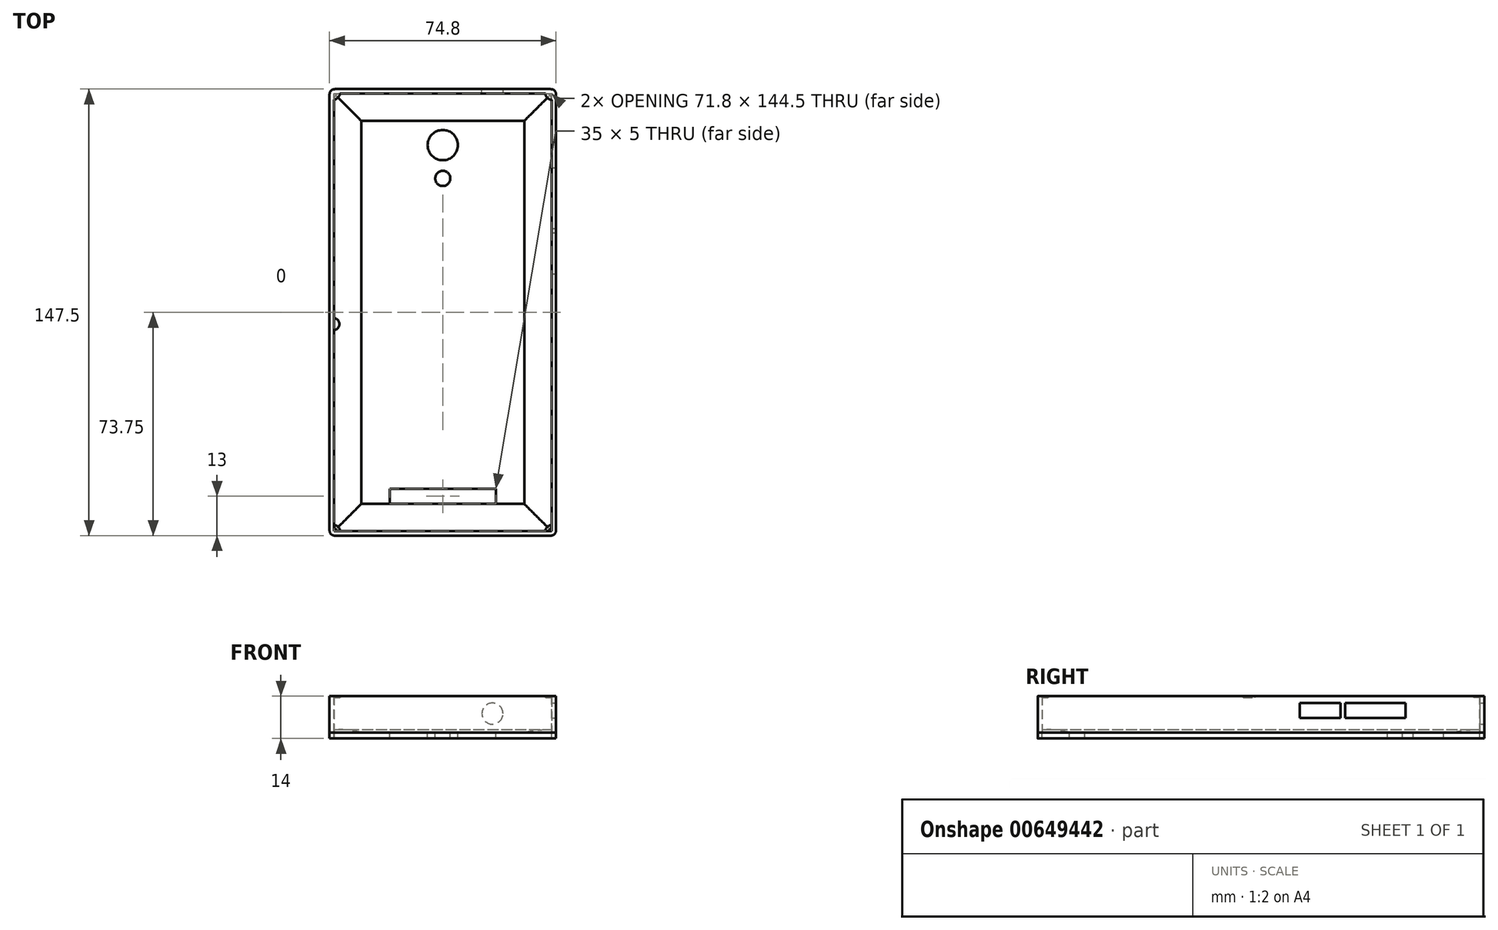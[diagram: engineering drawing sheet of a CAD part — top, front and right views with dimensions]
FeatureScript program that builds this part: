
annotation { "Feature Type Name" : "Feature", "Feature Type Description" : "" }
export const myFeature = defineFeature(function(context is Context, id is Id, definition is map)
    precondition{}
    {
        {
            var Q0;
            Q0=qCreatedBy(makeId("Top.planeOp"),FACE);
            var sketch = newSketch(context, id + "F0", { "sketchPlane" : qUnion([Q0])});
            skLineSegment(sketch, "E0.bottom", {"start": v(0, 0) * mm, "end": v(71.8, 0) * mm});
            skLineSegment(sketch, "E0.top", {"start": v(0, 144.5) * mm, "end": v(71.8, 144.5) * mm});
            skLineSegment(sketch, "E0.left", {"start": v(0, 0) * mm, "end": v(0, 144.5) * mm});
            skLineSegment(sketch, "E0.right", {"start": v(71.8, 0) * mm, "end": v(71.8, 144.5) * mm});
            skLineSegment(sketch, "E1", {"start": v(35.9, 9) * mm, "end": v(53.4, 9) * mm});
            skLineSegment(sketch, "E2", {"start": v(53.4, 9) * mm, "end": v(18.4, 9) * mm});
            skLineSegment(sketch, "E3", {"start": v(18.4, 9) * mm, "end": v(18.4, 14) * mm});
            skLineSegment(sketch, "E4", {"start": v(18.4, 14) * mm, "end": v(53.4, 14) * mm});
            skLineSegment(sketch, "E5", {"start": v(53.4, 14) * mm, "end": v(53.4, 9) * mm});
            skCircle(sketch, "E6", {"center": v(35.9, 127.5) * mm, "radius": 5 * mm});
            skCircle(sketch, "E7", {"center": v(35.9, 116.5) * mm, "radius": 2.5 * mm});
            skLineSegment(sketch, "E8", {"start": v(9, 110.42) * mm, "end": v(9, 9) * mm});
            skLineSegment(sketch, "E9", {"start": v(9, 9) * mm, "end": v(62.8, 9) * mm});
            skLineSegment(sketch, "E10", {"start": v(62.8, 9) * mm, "end": v(62.8, 135.5) * mm});
            skLineSegment(sketch, "E11", {"start": v(62.8, 135.5) * mm, "end": v(9, 135.5) * mm});
            skLineSegment(sketch, "E12", {"start": v(9, 135.5) * mm, "end": v(9, 110.42) * mm});
            skLineSegment(sketch, "E13.0", {"start": v(-1.5, -1.5) * mm, "end": v(-1.5, 146) * mm});
            skLineSegment(sketch, "E13.1", {"start": v(-1.5, -1.5) * mm, "end": v(73.3, -1.5) * mm});
            skLineSegment(sketch, "E13.2", {"start": v(73.3, -1.5) * mm, "end": v(73.3, 146) * mm});
            skLineSegment(sketch, "E13.3", {"start": v(-1.5, 146) * mm, "end": v(73.3, 146) * mm});
            skSolve(sketch);
        }
        {
            var Q0;
            Q0=makeQuery(id+"F0.imprint","IMPRINT",FACE,{"disambiguationData":[TD([[makeQuery(id+"F0.imprint","IMPRINT",EDGE,{"derivedFrom":sQuery(id+"F0.wireOp",EDGE,"E0.bottom")}),-1.0]])]});
            extrude(context, id + "F1", {"entities" : qUnion([Q0]), "depth" : 12 * mm, "offsetDistance" : 25 * mm});
        }
        {
            var Q0;
            Q0=makeQuery(id+"F0.imprint","IMPRINT",FACE,{"disambiguationData":[TD([[makeQuery(id+"F0.imprint","IMPRINT",EDGE,{"derivedFrom":sQuery(id+"F0.wireOp",EDGE,"E0.bottom")}),1.0]])]});
            var Q1;
            {var subQ3=sQuery(id+"F0.wireOp",EDGE,"E3");Q1=makeQuery(id+"F0.imprint","IMPRINT",FACE,{"disambiguationData":[TD([[makeQuery(id+"F0.imprint","IMPRINT",EDGE,{"derivedFrom":subQ3}),1.0]])]});}
            extrude(context, id + "F2", {"entities" : qUnion([Q0, Q1]), "operationType" : NewBodyOperationType.ADD, "oppositeDirection" : true, "depth" : 2 * mm, "offsetDistance" : 25 * mm});
        }
        {
            var Q0;
            Q0=makeQuery(id+"F1.opExtrude","SWEPT_EDGE",EDGE,{"disambiguationData":[OSD([sQuery(id+"F0.wireOp",EDGE,"E13.0"),sQuery(id+"F0.wireOp",EDGE,"E13.3")])]});
            var Q1;
            Q1=makeQuery(id+"F1.opExtrude","SWEPT_EDGE",EDGE,{"disambiguationData":[OSD([sQuery(id+"F0.wireOp",EDGE,"E13.2"),sQuery(id+"F0.wireOp",EDGE,"E13.3")])]});
            var Q2;
            Q2=makeQuery(id+"F1.opExtrude","SWEPT_EDGE",EDGE,{"disambiguationData":[OSD([sQuery(id+"F0.wireOp",EDGE,"E13.1"),sQuery(id+"F0.wireOp",EDGE,"E13.2")])]});
            var Q3;
            Q3=makeQuery(id+"F1.opExtrude","SWEPT_EDGE",EDGE,{"disambiguationData":[OSD([sQuery(id+"F0.wireOp",EDGE,"E13.0"),sQuery(id+"F0.wireOp",EDGE,"E13.1")])]});
            var Q4;
            Q4=makeQuery(id+"F1.opExtrude","SWEPT_EDGE",EDGE,{"disambiguationData":[OSD([sQuery(id+"F0.wireOp",EDGE,"E0.bottom"),sQuery(id+"F0.wireOp",EDGE,"E0.left")])]});
            var Q5;
            Q5=makeQuery(id+"F1.opExtrude","SWEPT_EDGE",EDGE,{"disambiguationData":[OSD([sQuery(id+"F0.wireOp",EDGE,"E0.bottom"),sQuery(id+"F0.wireOp",EDGE,"E0.right")])]});
            var Q6;
            Q6=makeQuery(id+"F1.opExtrude","SWEPT_EDGE",EDGE,{"disambiguationData":[OSD([sQuery(id+"F0.wireOp",EDGE,"E0.top"),sQuery(id+"F0.wireOp",EDGE,"E0.right")])]});
            var Q7;
            Q7=makeQuery(id+"F1.opExtrude","SWEPT_EDGE",EDGE,{"disambiguationData":[OSD([sQuery(id+"F0.wireOp",EDGE,"E0.top"),sQuery(id+"F0.wireOp",EDGE,"E0.left")])]});
            fillet(context, id + "F3", {"entities" : qUnion([Q0, Q1, Q2, Q3, Q4, Q5, Q6, Q7]), "radius" : 2 * mm, "tangentPropagation" : true, "rho" : 0.5, "crossSection" : FilletCrossSection.CONIC, "allowEdgeOverflow" : false});
        }
        {
            var Q0;
            Q0=makeQuery(id+"F1.opExtrude","CAP_FACE",FACE,{"disambiguationData":[OSD([sQuery(id+"F0.wireOp",EDGE,"E0.bottom"),sQuery(id+"F0.wireOp",EDGE,"E0.top"),sQuery(id+"F0.wireOp",EDGE,"E0.left"),sQuery(id+"F0.wireOp",EDGE,"E0.right"),sQuery(id+"F0.wireOp",EDGE,"E13.0"),sQuery(id+"F0.wireOp",EDGE,"E13.1"),sQuery(id+"F0.wireOp",EDGE,"E13.2"),sQuery(id+"F0.wireOp",EDGE,"E13.3")])],"isStart":true});
            extrude(context, id + "F4", {"entities" : qUnion([Q0]), "depth" : 2 * mm, "offsetDistance" : 25 * mm});
        }
        {
            var Q0;
            Q0=makeQuery(id+"F0.imprint","IMPRINT",FACE,{"disambiguationData":[TD([[makeQuery(id+"F0.imprint","IMPRINT",EDGE,{"derivedFrom":sQuery(id+"F0.wireOp",EDGE,"E0.bottom")}),1.0]])]});
            extrude(context, id + "F5", {"entities" : qUnion([Q0]), "depth" : 1 * mm, "offsetDistance" : 25 * mm});
        }
        {
            var Q0;
            Q0=makeQuery(id+"F5.opExtrude","CAP_EDGE",EDGE,{"disambiguationData":[OSD([sQuery(id+"F0.wireOp",EDGE,"E10")])],"isStart":false});
            var Q1;
            Q1=makeQuery(id+"F5.opExtrude","CAP_EDGE",EDGE,{"disambiguationData":[OSD([sQuery(id+"F0.wireOp",EDGE,"E9")])],"isStart":false});
            var Q2;
            Q2=makeQuery(id+"F5.opExtrude","CAP_EDGE",EDGE,{"disambiguationData":[OSD([sQuery(id+"F0.wireOp",EDGE,"E8"),sQuery(id+"F0.wireOp",EDGE,"E12")])],"isStart":false});
            var Q3;
            Q3=makeQuery(id+"F5.opExtrude","CAP_EDGE",EDGE,{"disambiguationData":[OSD([sQuery(id+"F0.wireOp",EDGE,"E11")])],"isStart":false});
            fillet(context, id + "F6", {"entities" : qUnion([Q0, Q1, Q2, Q3]), "radius" : 35 * mm, "tangentPropagation" : true, "allowEdgeOverflow" : false});
        }
        {
            var Q0;
            Q0=makeQuery(id+"F1.opExtrude","SWEPT_FACE",FACE,{"disambiguationData":[OSD([sQuery(id+"F0.wireOp",EDGE,"E13.2")])]});
            var sketch = newSketch(context, id + "F7", { "sketchPlane" : qUnion([Q0])});
            skLineSegment(sketch, "E14.bottom", {"start": v(85, 9.75) * mm, "end": v(120, 9.75) * mm});
            skLineSegment(sketch, "E14.top", {"start": v(85, 4.75) * mm, "end": v(120, 4.75) * mm});
            skLineSegment(sketch, "E14.left", {"start": v(85, 9.75) * mm, "end": v(85, 4.75) * mm});
            skLineSegment(sketch, "E14.right", {"start": v(120, 9.75) * mm, "end": v(120, 4.75) * mm});
            skLineSegment(sketch, "E15", {"start": v(100, 9.75) * mm, "end": v(100, 4.75) * mm});
            skLineSegment(sketch, "E16", {"start": v(98.5, 9.75) * mm, "end": v(98.5, 4.75) * mm});
            skSolve(sketch);
        }
        {
            var Q0;
            {var subQ0=sQuery(id+"F7.wireOp",EDGE,"E14.left");Q0=makeQuery(id+"F7.imprint","IMPRINT",FACE,{"disambiguationData":[TD([[makeQuery(id+"F7.imprint","IMPRINT",EDGE,{"derivedFrom":subQ0}),1.0]])]});}
            var Q1;
            {var subQ0=sQuery(id+"F7.wireOp",EDGE,"E14.right");Q1=makeQuery(id+"F7.imprint","IMPRINT",FACE,{"disambiguationData":[TD([[makeQuery(id+"F7.imprint","IMPRINT",EDGE,{"derivedFrom":subQ0}),-1.0]])]});}
            extrude(context, id + "F8", {"entities" : qUnion([Q0, Q1]), "operationType" : NewBodyOperationType.REMOVE, "oppositeDirection" : true, "depth" : 25 * mm, "offsetDistance" : 25 * mm});
        }
        {
            var Q0;
            Q0=makeQuery(id+"F1.opExtrude","SWEPT_FACE",FACE,{"disambiguationData":[OSD([sQuery(id+"F0.wireOp",EDGE,"E13.3")])]});
            var sketch = newSketch(context, id + "F9", { "sketchPlane" : qUnion([Q0])});
            skCircle(sketch, "E17", {"center": v(-52.3, 6.23) * mm, "radius": 3.5 * mm});
            skSolve(sketch);
        }
        {
            var Q0;
            Q0=makeQuery(id+"F9.imprint","IMPRINT",FACE,{"disambiguationData":[TD([[makeQuery(id+"F9.imprint","IMPRINT",EDGE,{"derivedFrom":sQuery(id+"F9.wireOp",EDGE,"E17")}),1.0]])]});
            extrude(context, id + "F10", {"entities" : qUnion([Q0]), "operationType" : NewBodyOperationType.REMOVE, "oppositeDirection" : true, "depth" : 25 * mm, "offsetDistance" : 25 * mm});
        }
        {
            var Q0;
            Q0=makeQuery(id+"F1.opExtrude","CAP_FACE",FACE,{"disambiguationData":[OSD([sQuery(id+"F0.wireOp",EDGE,"E0.bottom"),sQuery(id+"F0.wireOp",EDGE,"E0.top"),sQuery(id+"F0.wireOp",EDGE,"E0.left"),sQuery(id+"F0.wireOp",EDGE,"E0.right"),sQuery(id+"F0.wireOp",EDGE,"E13.0"),sQuery(id+"F0.wireOp",EDGE,"E13.1"),sQuery(id+"F0.wireOp",EDGE,"E13.2"),sQuery(id+"F0.wireOp",EDGE,"E13.3")])],"isStart":false});
            var sketch = newSketch(context, id + "F11", { "sketchPlane" : qUnion([Q0])});
            skArc(sketch, "E18", {"start": v(0, 142.5) * mm, "mid": v(1.3, 143.2) * mm, "end": v(2, 144.5) * mm});
            skArc(sketch, "E19", {"start": v(69.8, 144.5) * mm, "mid": v(70.39, 143.09) * mm, "end": v(71.8, 142.5) * mm});
            skArc(sketch, "E20", {"start": v(71.8, 2) * mm, "mid": v(70.4, 1.4) * mm, "end": v(69.8, 0) * mm});
            skArc(sketch, "E21", {"start": v(2, 0) * mm, "mid": v(1.4, 1.4) * mm, "end": v(0, 2) * mm});
            skSolve(sketch);
        }
        {
            var Q0;
            Q0 = qSketchRegion(id + "F11", true);
            var Q1;
            Q1=makeQuery(id+"F11.imprint","IMPRINT",FACE,{"disambiguationData":[TD([[makeQuery(id+"F11.imprint","IMPRINT",EDGE,{"derivedFrom":sQuery(id+"F11.wireOp",EDGE,"E18")}),1.0]])]});
            var Q2;
            Q2=makeQuery(id+"F11.imprint","IMPRINT",FACE,{"disambiguationData":[TD([[makeQuery(id+"F11.imprint","IMPRINT",EDGE,{"derivedFrom":sQuery(id+"F11.wireOp",EDGE,"E19")}),1.0]])]});
            extrude(context, id + "F12", {"entities" : qUnion([Q0, Q1, Q2]), "operationType" : NewBodyOperationType.ADD, "oppositeDirection" : true, "depth" : 0.5 * mm, "offsetDistance" : 25 * mm});
        }
        {
            var Q0;
            {var subQ0=sQuery(id+"F0.wireOp",EDGE,"E13.3");var subQ1=sQuery(id+"F0.wireOp",EDGE,"E13.2");var subQ2=sQuery(id+"F0.wireOp",EDGE,"E13.1");var subQ3=sQuery(id+"F0.wireOp",EDGE,"E13.0");var subQ4=sQuery(id+"F0.wireOp",EDGE,"E0.right");var subQ5=sQuery(id+"F0.wireOp",EDGE,"E0.left");var subQ6=sQuery(id+"F0.wireOp",EDGE,"E0.top");var subQ7=sQuery(id+"F0.wireOp",EDGE,"E0.bottom");Q0=makeQuery(id+"F12.boolean.opBoolean","MERGE",FACE,{"derivedFrom":[makeQuery(id+"F1.opExtrude","CAP_FACE",FACE,{"disambiguationData":[OSD([subQ7,subQ6,subQ5,subQ4,subQ3,subQ2,subQ1,subQ0])],"isStart":false}),makeQuery(id+"F12.opExtrude","CAP_FACE",FACE,{"disambiguationData":[OSD([subQ7,subQ6,subQ5,subQ4,subQ3,subQ2,subQ1,subQ0,sQuery(id+"F11.wireOp",EDGE,"E18")])],"isStart":true}),makeQuery(id+"F12.opExtrude","CAP_FACE",FACE,{"disambiguationData":[OSD([subQ7,subQ6,subQ5,subQ4,subQ3,subQ2,subQ1,subQ0,sQuery(id+"F11.wireOp",EDGE,"E19")])],"isStart":true})]});}
            var sketch = newSketch(context, id + "F13", { "sketchPlane" : qUnion([Q0])});
            skArc(sketch, "E22", {"start": v(2, 0) * mm, "mid": v(1.4, 1.4) * mm, "end": v(0, 2) * mm});
            skArc(sketch, "E23", {"start": v(71.8, 2) * mm, "mid": v(70.39, 1.41) * mm, "end": v(69.8, 0) * mm});
            skSolve(sketch);
        }
        {
            var Q0;
            Q0=makeQuery(id+"F13.imprint","IMPRINT",FACE,{"disambiguationData":[TD([[makeQuery(id+"F13.imprint","IMPRINT",EDGE,{"derivedFrom":sQuery(id+"F13.wireOp",EDGE,"E23")}),1.0]])]});
            var Q1;
            Q1=makeQuery(id+"F13.imprint","IMPRINT",FACE,{"disambiguationData":[TD([[makeQuery(id+"F13.imprint","IMPRINT",EDGE,{"derivedFrom":sQuery(id+"F13.wireOp",EDGE,"E22")}),1.0]])]});
            extrude(context, id + "F14", {"entities" : qUnion([Q0, Q1]), "oppositeDirection" : true, "depth" : 0.5 * mm, "offsetDistance" : 25 * mm});
        }
        {
            var Q0;
            {var subQ0=sQuery(id+"F0.wireOp",EDGE,"E13.3");var subQ1=sQuery(id+"F0.wireOp",EDGE,"E13.2");var subQ2=sQuery(id+"F0.wireOp",EDGE,"E13.1");var subQ3=sQuery(id+"F0.wireOp",EDGE,"E13.0");var subQ4=sQuery(id+"F0.wireOp",EDGE,"E0.right");var subQ5=sQuery(id+"F0.wireOp",EDGE,"E0.left");var subQ6=sQuery(id+"F0.wireOp",EDGE,"E0.top");var subQ7=sQuery(id+"F0.wireOp",EDGE,"E0.bottom");Q0=makeQuery(id+"F12.boolean.opBoolean","MERGE",FACE,{"derivedFrom":[makeQuery(id+"F1.opExtrude","CAP_FACE",FACE,{"disambiguationData":[OSD([subQ7,subQ6,subQ5,subQ4,subQ3,subQ2,subQ1,subQ0])],"isStart":false}),makeQuery(id+"F12.opExtrude","CAP_FACE",FACE,{"disambiguationData":[OSD([subQ7,subQ6,subQ5,subQ4,subQ3,subQ2,subQ1,subQ0,sQuery(id+"F11.wireOp",EDGE,"E18")])],"isStart":true}),makeQuery(id+"F12.opExtrude","CAP_FACE",FACE,{"disambiguationData":[OSD([subQ7,subQ6,subQ5,subQ4,subQ3,subQ2,subQ1,subQ0,sQuery(id+"F11.wireOp",EDGE,"E19")])],"isStart":true})]});}
            var sketch = newSketch(context, id + "F15", { "sketchPlane" : qUnion([Q0])});
            skArc(sketch, "E24", {"start": v(0, 66.39) * mm, "mid": v(1.76, 68.38) * mm, "end": v(0, 70.36) * mm});
            skSolve(sketch);
        }
        {
            var Q0;
            Q0 = qSketchRegion(id + "F15", true);
            var Q1;
            {var subQ0=sQuery(id+"F15.wireOp",EDGE,"E24");Q1=makeQuery(id+"F15.imprint","IMPRINT",FACE,{"disambiguationData":[TD([[makeQuery(id+"F15.imprint","IMPRINT",EDGE,{"derivedFrom":subQ0}),1.0]])]});}
            extrude(context, id + "F16", {"entities" : qUnion([Q0, Q1]), "oppositeDirection" : true, "depth" : 0.5 * mm, "offsetDistance" : 25 * mm});
        }
    });
